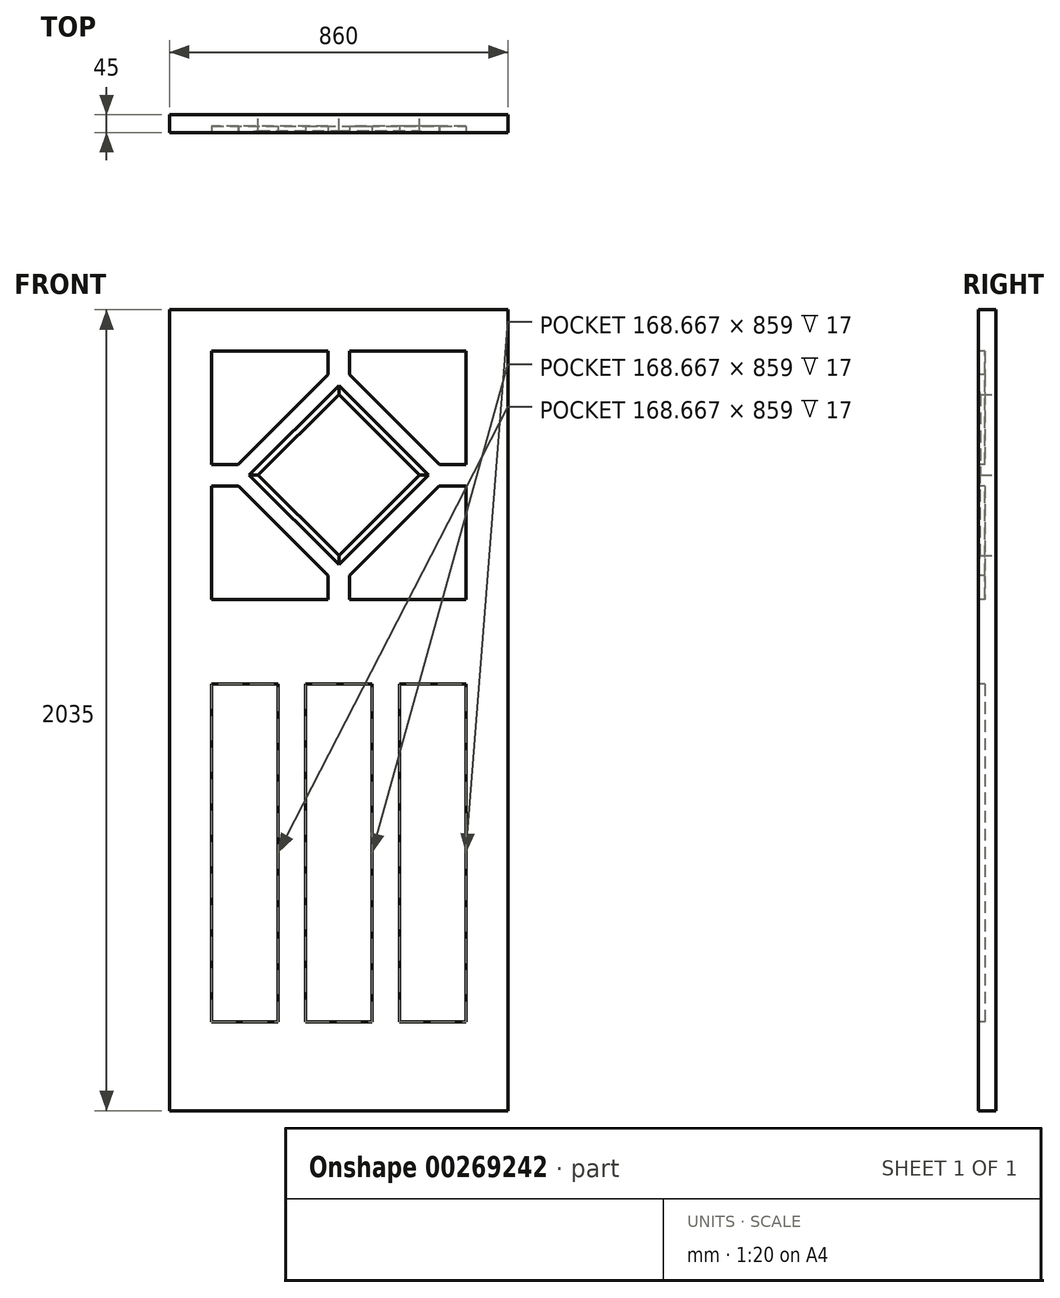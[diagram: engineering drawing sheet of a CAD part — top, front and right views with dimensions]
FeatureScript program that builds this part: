
annotation { "Feature Type Name" : "Feature", "Feature Type Description" : "" }
export const myFeature = defineFeature(function(context is Context, id is Id, definition is map)
    precondition{}
    {
        {
            var Q0;
            Q0=qCreatedBy(makeId("Front.planeOp"),FACE);
            var sketch = newSketch(context, id + "F0", { "sketchPlane" : qUnion([Q0])});
            skLineSegment(sketch, "E0.bottom", {"start": v(-430, 1017.5) * mm, "end": v(430, 1017.5) * mm});
            skLineSegment(sketch, "E0.top", {"start": v(-430, -1017.5) * mm, "end": v(430, -1017.5) * mm});
            skLineSegment(sketch, "E0.left", {"start": v(-430, 1017.5) * mm, "end": v(-430, -1017.5) * mm});
            skLineSegment(sketch, "E0.right", {"start": v(430, 1017.5) * mm, "end": v(430, -1017.5) * mm});
            skPoint(sketch, "E0.middle", {"position": v(0, 0) * mm});
            skLineSegment(sketch, "E1", {"start": v(0, 392.38) * mm, "end": v(-205.06, 597.44) * mm});
            skLineSegment(sketch, "E2", {"start": v(-205.06, 597.44) * mm, "end": v(0, 802.5) * mm});
            skLineSegment(sketch, "E3", {"start": v(0, 802.5) * mm, "end": v(205.06, 597.44) * mm});
            skLineSegment(sketch, "E4", {"start": v(205.06, 597.44) * mm, "end": v(0, 392.38) * mm});
            skSolve(sketch);
        }
        {
            var Q0;
            Q0=makeQuery(id+"F0.imprint","IMPRINT",FACE,{"disambiguationData":[TD([[makeQuery(id+"F0.imprint","IMPRINT",EDGE,{"derivedFrom":sQuery(id+"F0.wireOp",EDGE,"E0.bottom")}),-1.0]])]});
            extrude(context, id + "F1", {"entities" : qUnion([Q0]), "endBound" : BoundingType.SYMMETRIC, "depth" : 45 * mm});
        }
        {
            var Q0;
            Q0=makeQuery(id+"F1.opExtrude","CAP_FACE",FACE,{"disambiguationData":[OSD([sQuery(id+"F0.wireOp",EDGE,"E0.bottom"),sQuery(id+"F0.wireOp",EDGE,"E0.top"),sQuery(id+"F0.wireOp",EDGE,"E0.left"),sQuery(id+"F0.wireOp",EDGE,"E0.right"),sQuery(id+"F0.wireOp",EDGE,"E1"),sQuery(id+"F0.wireOp",EDGE,"E2"),sQuery(id+"F0.wireOp",EDGE,"E3"),sQuery(id+"F0.wireOp",EDGE,"E4")])],"isStart":false});
            var sketch = newSketch(context, id + "F2", { "sketchPlane" : qUnion([Q0])});
            skLineSegment(sketch, "E5", {"start": v(-323, 624.5) * mm, "end": v(-323, 912.5) * mm});
            skLineSegment(sketch, "E6", {"start": v(-323, 912.5) * mm, "end": v(-27.5, 912.5) * mm});
            skLineSegment(sketch, "E7", {"start": v(-27.5, 912.5) * mm, "end": v(-27.5, 852.78) * mm});
            skLineSegment(sketch, "E8", {"start": v(-27.5, 852.78) * mm, "end": v(-255.78, 624.5) * mm});
            skLineSegment(sketch, "E9", {"start": v(-255.78, 624.5) * mm, "end": v(-323, 624.5) * mm});
            skLineSegment(sketch, "E10", {"start": v(27.5, 912.5) * mm, "end": v(27.5, 852.78) * mm});
            skLineSegment(sketch, "E11", {"start": v(27.5, 852.78) * mm, "end": v(255.78, 624.5) * mm});
            skLineSegment(sketch, "E12", {"start": v(255.78, 624.5) * mm, "end": v(323, 624.5) * mm});
            skLineSegment(sketch, "E13", {"start": v(323, 624.5) * mm, "end": v(323, 912.5) * mm});
            skLineSegment(sketch, "E14", {"start": v(323, 912.5) * mm, "end": v(27.5, 912.5) * mm});
            skLineSegment(sketch, "E15", {"start": v(-323, 569.5) * mm, "end": v(-323, 281.5) * mm});
            skLineSegment(sketch, "E16", {"start": v(-323, 281.5) * mm, "end": v(-27.5, 281.5) * mm});
            skLineSegment(sketch, "E17", {"start": v(-27.5, 281.5) * mm, "end": v(-27.5, 342.1) * mm});
            skLineSegment(sketch, "E18", {"start": v(-27.5, 342.1) * mm, "end": v(-254.9, 569.5) * mm});
            skLineSegment(sketch, "E19", {"start": v(-254.9, 569.5) * mm, "end": v(-323, 569.5) * mm});
            skLineSegment(sketch, "E20", {"start": v(27.5, 281.5) * mm, "end": v(323, 281.5) * mm});
            skLineSegment(sketch, "E21", {"start": v(323, 281.5) * mm, "end": v(323, 569.5) * mm});
            skLineSegment(sketch, "E22", {"start": v(323, 569.5) * mm, "end": v(254.9, 569.5) * mm});
            skLineSegment(sketch, "E23", {"start": v(254.9, 569.5) * mm, "end": v(27.5, 342.1) * mm});
            skLineSegment(sketch, "E24", {"start": v(27.5, 342.1) * mm, "end": v(27.5, 281.5) * mm});
            skLineSegment(sketch, "E25.bottom", {"start": v(-323, 66.5) * mm, "end": v(-154.33, 66.5) * mm});
            skLineSegment(sketch, "E25.top", {"start": v(-323, -792.5) * mm, "end": v(-154.33, -792.5) * mm});
            skLineSegment(sketch, "E25.left", {"start": v(-323, 66.5) * mm, "end": v(-323, -792.5) * mm});
            skLineSegment(sketch, "E25.right", {"start": v(-154.33, 66.5) * mm, "end": v(-154.33, -792.5) * mm});
            skLineSegment(sketch, "E26.bottom", {"start": v(323, 66.5) * mm, "end": v(154.33, 66.5) * mm});
            skLineSegment(sketch, "E26.top", {"start": v(323, -792.5) * mm, "end": v(154.33, -792.5) * mm});
            skLineSegment(sketch, "E26.left", {"start": v(323, 66.5) * mm, "end": v(323, -792.5) * mm});
            skLineSegment(sketch, "E26.right", {"start": v(154.33, 66.5) * mm, "end": v(154.33, -792.5) * mm});
            skLineSegment(sketch, "E27.bottom", {"start": v(-84.33, 66.5) * mm, "end": v(84.33, 66.5) * mm});
            skLineSegment(sketch, "E27.top", {"start": v(-84.33, -792.5) * mm, "end": v(84.33, -792.5) * mm});
            skLineSegment(sketch, "E27.left", {"start": v(-84.33, 66.5) * mm, "end": v(-84.33, -792.5) * mm});
            skLineSegment(sketch, "E27.right", {"start": v(84.33, 66.5) * mm, "end": v(84.33, -792.5) * mm});
            skSolve(sketch);
        }
        {
            var Q0;
            Q0=makeQuery(id+"F2.imprint","IMPRINT",FACE,{"disambiguationData":[TD([[makeQuery(id+"F2.imprint","IMPRINT",EDGE,{"derivedFrom":sQuery(id+"F2.wireOp",EDGE,"E5")}),-1.0]])]});
            var Q1;
            Q1=makeQuery(id+"F2.imprint","IMPRINT",FACE,{"disambiguationData":[TD([[makeQuery(id+"F2.imprint","IMPRINT",EDGE,{"derivedFrom":sQuery(id+"F2.wireOp",EDGE,"E10")}),1.0]])]});
            var Q2;
            Q2=makeQuery(id+"F2.imprint","IMPRINT",FACE,{"disambiguationData":[TD([[makeQuery(id+"F2.imprint","IMPRINT",EDGE,{"derivedFrom":sQuery(id+"F2.wireOp",EDGE,"E20")}),1.0]])]});
            var Q3;
            Q3=makeQuery(id+"F2.imprint","IMPRINT",FACE,{"disambiguationData":[TD([[makeQuery(id+"F2.imprint","IMPRINT",EDGE,{"derivedFrom":sQuery(id+"F2.wireOp",EDGE,"E15")}),1.0]])]});
            var Q4;
            Q4=makeQuery(id+"F2.imprint","IMPRINT",FACE,{"disambiguationData":[TD([[makeQuery(id+"F2.imprint","IMPRINT",EDGE,{"derivedFrom":sQuery(id+"F2.wireOp",EDGE,"E25.bottom")}),-1.0]])]});
            var Q5;
            Q5=makeQuery(id+"F2.imprint","IMPRINT",FACE,{"disambiguationData":[TD([[makeQuery(id+"F2.imprint","IMPRINT",EDGE,{"derivedFrom":sQuery(id+"F2.wireOp",EDGE,"E27.bottom")}),-1.0]])]});
            var Q6;
            Q6=makeQuery(id+"F2.imprint","IMPRINT",FACE,{"disambiguationData":[TD([[makeQuery(id+"F2.imprint","IMPRINT",EDGE,{"derivedFrom":sQuery(id+"F2.wireOp",EDGE,"E26.bottom")}),1.0]])]});
            extrude(context, id + "F3", {"entities" : qUnion([Q0, Q1, Q2, Q3, Q4, Q5, Q6]), "operationType" : NewBodyOperationType.REMOVE, "oppositeDirection" : true, "depth" : 17 * mm});
        }
        {
            var Q0;
            Q0=makeQuery(id+"F3.boolean.opBoolean","COPY",EDGE,{"derivedFrom":makeQuery(id+"F3.opExtrude","CAP_EDGE",EDGE,{"disambiguationData":[OSD([sQuery(id+"F2.wireOp",EDGE,"E25.left")])],"isStart":true})});
            var Q1;
            Q1=makeQuery(id+"F3.boolean.opBoolean","COPY",EDGE,{"derivedFrom":makeQuery(id+"F3.opExtrude","CAP_EDGE",EDGE,{"disambiguationData":[OSD([sQuery(id+"F2.wireOp",EDGE,"E25.bottom")])],"isStart":true})});
            var Q2;
            Q2=makeQuery(id+"F3.boolean.opBoolean","COPY",EDGE,{"derivedFrom":makeQuery(id+"F3.opExtrude","CAP_EDGE",EDGE,{"disambiguationData":[OSD([sQuery(id+"F2.wireOp",EDGE,"E25.right")])],"isStart":true})});
            var Q3;
            Q3=makeQuery(id+"F3.boolean.opBoolean","COPY",EDGE,{"derivedFrom":makeQuery(id+"F3.opExtrude","CAP_EDGE",EDGE,{"disambiguationData":[OSD([sQuery(id+"F2.wireOp",EDGE,"E25.top")])],"isStart":true})});
            var Q4;
            Q4=makeQuery(id+"F3.boolean.opBoolean","COPY",EDGE,{"derivedFrom":makeQuery(id+"F3.opExtrude","CAP_EDGE",EDGE,{"disambiguationData":[OSD([sQuery(id+"F2.wireOp",EDGE,"E27.left")])],"isStart":true})});
            var Q5;
            Q5=makeQuery(id+"F3.boolean.opBoolean","COPY",EDGE,{"derivedFrom":makeQuery(id+"F3.opExtrude","CAP_EDGE",EDGE,{"disambiguationData":[OSD([sQuery(id+"F2.wireOp",EDGE,"E27.top")])],"isStart":true})});
            var Q6;
            Q6=makeQuery(id+"F3.boolean.opBoolean","COPY",EDGE,{"derivedFrom":makeQuery(id+"F3.opExtrude","CAP_EDGE",EDGE,{"disambiguationData":[OSD([sQuery(id+"F2.wireOp",EDGE,"E27.right")])],"isStart":true})});
            var Q7;
            Q7=makeQuery(id+"F3.boolean.opBoolean","COPY",EDGE,{"derivedFrom":makeQuery(id+"F3.opExtrude","CAP_EDGE",EDGE,{"disambiguationData":[OSD([sQuery(id+"F2.wireOp",EDGE,"E26.right")])],"isStart":true})});
            var Q8;
            Q8=makeQuery(id+"F3.boolean.opBoolean","COPY",EDGE,{"derivedFrom":makeQuery(id+"F3.opExtrude","CAP_EDGE",EDGE,{"disambiguationData":[OSD([sQuery(id+"F2.wireOp",EDGE,"E26.top")])],"isStart":true})});
            var Q9;
            Q9=makeQuery(id+"F3.boolean.opBoolean","COPY",EDGE,{"derivedFrom":makeQuery(id+"F3.opExtrude","CAP_EDGE",EDGE,{"disambiguationData":[OSD([sQuery(id+"F2.wireOp",EDGE,"E26.left")])],"isStart":true})});
            var Q10;
            Q10=makeQuery(id+"F3.boolean.opBoolean","COPY",EDGE,{"derivedFrom":makeQuery(id+"F3.opExtrude","CAP_EDGE",EDGE,{"disambiguationData":[OSD([sQuery(id+"F2.wireOp",EDGE,"E26.bottom")])],"isStart":true})});
            var Q11;
            Q11=makeQuery(id+"F3.boolean.opBoolean","COPY",EDGE,{"derivedFrom":makeQuery(id+"F3.opExtrude","CAP_EDGE",EDGE,{"disambiguationData":[OSD([sQuery(id+"F2.wireOp",EDGE,"E27.bottom")])],"isStart":true})});
            var Q12;
            Q12=makeQuery(id+"F3.boolean.opBoolean","COPY",EDGE,{"derivedFrom":makeQuery(id+"F3.opExtrude","CAP_EDGE",EDGE,{"disambiguationData":[OSD([sQuery(id+"F2.wireOp",EDGE,"E20")])],"isStart":true})});
            var Q13;
            Q13=makeQuery(id+"F3.boolean.opBoolean","COPY",EDGE,{"derivedFrom":makeQuery(id+"F3.opExtrude","CAP_EDGE",EDGE,{"disambiguationData":[OSD([sQuery(id+"F2.wireOp",EDGE,"E21")])],"isStart":true})});
            var Q14;
            Q14=makeQuery(id+"F3.boolean.opBoolean","COPY",EDGE,{"derivedFrom":makeQuery(id+"F3.opExtrude","CAP_EDGE",EDGE,{"disambiguationData":[OSD([sQuery(id+"F2.wireOp",EDGE,"E22")])],"isStart":true})});
            var Q15;
            Q15=makeQuery(id+"F3.boolean.opBoolean","COPY",EDGE,{"derivedFrom":makeQuery(id+"F3.opExtrude","CAP_EDGE",EDGE,{"disambiguationData":[OSD([sQuery(id+"F2.wireOp",EDGE,"E12")])],"isStart":true})});
            var Q16;
            Q16=makeQuery(id+"F3.boolean.opBoolean","COPY",EDGE,{"derivedFrom":makeQuery(id+"F3.opExtrude","CAP_EDGE",EDGE,{"disambiguationData":[OSD([sQuery(id+"F2.wireOp",EDGE,"E13")])],"isStart":true})});
            var Q17;
            Q17=makeQuery(id+"F3.boolean.opBoolean","COPY",EDGE,{"derivedFrom":makeQuery(id+"F3.opExtrude","CAP_EDGE",EDGE,{"disambiguationData":[OSD([sQuery(id+"F2.wireOp",EDGE,"E17")])],"isStart":true})});
            var Q18;
            Q18=makeQuery(id+"F3.boolean.opBoolean","COPY",EDGE,{"derivedFrom":makeQuery(id+"F3.opExtrude","CAP_EDGE",EDGE,{"disambiguationData":[OSD([sQuery(id+"F2.wireOp",EDGE,"E16")])],"isStart":true})});
            var Q19;
            Q19=makeQuery(id+"F3.boolean.opBoolean","COPY",EDGE,{"derivedFrom":makeQuery(id+"F3.opExtrude","CAP_EDGE",EDGE,{"disambiguationData":[OSD([sQuery(id+"F2.wireOp",EDGE,"E8")])],"isStart":true})});
            var Q20;
            Q20=makeQuery(id+"F3.boolean.opBoolean","COPY",EDGE,{"derivedFrom":makeQuery(id+"F3.opExtrude","CAP_EDGE",EDGE,{"disambiguationData":[OSD([sQuery(id+"F2.wireOp",EDGE,"E9")])],"isStart":true})});
            var Q21;
            Q21=makeQuery(id+"F3.boolean.opBoolean","COPY",EDGE,{"derivedFrom":makeQuery(id+"F3.opExtrude","CAP_EDGE",EDGE,{"disambiguationData":[OSD([sQuery(id+"F2.wireOp",EDGE,"E14")])],"isStart":true})});
            var Q22;
            Q22=makeQuery(id+"F3.boolean.opBoolean","COPY",EDGE,{"derivedFrom":makeQuery(id+"F3.opExtrude","CAP_EDGE",EDGE,{"disambiguationData":[OSD([sQuery(id+"F2.wireOp",EDGE,"E23")])],"isStart":true})});
            var Q23;
            Q23=makeQuery(id+"F3.boolean.opBoolean","COPY",EDGE,{"derivedFrom":makeQuery(id+"F3.opExtrude","CAP_EDGE",EDGE,{"disambiguationData":[OSD([sQuery(id+"F2.wireOp",EDGE,"E7")])],"isStart":true})});
            var Q24;
            Q24=makeQuery(id+"F3.boolean.opBoolean","COPY",EDGE,{"derivedFrom":makeQuery(id+"F3.opExtrude","CAP_EDGE",EDGE,{"disambiguationData":[OSD([sQuery(id+"F2.wireOp",EDGE,"E6")])],"isStart":true})});
            var Q25;
            Q25=makeQuery(id+"F3.boolean.opBoolean","COPY",EDGE,{"derivedFrom":makeQuery(id+"F3.opExtrude","CAP_EDGE",EDGE,{"disambiguationData":[OSD([sQuery(id+"F2.wireOp",EDGE,"E19")])],"isStart":true})});
            var Q26;
            Q26=makeQuery(id+"F3.boolean.opBoolean","COPY",EDGE,{"derivedFrom":makeQuery(id+"F3.opExtrude","CAP_EDGE",EDGE,{"disambiguationData":[OSD([sQuery(id+"F2.wireOp",EDGE,"E18")])],"isStart":true})});
            var Q27;
            Q27=makeQuery(id+"F3.boolean.opBoolean","COPY",EDGE,{"derivedFrom":makeQuery(id+"F3.opExtrude","CAP_EDGE",EDGE,{"disambiguationData":[OSD([sQuery(id+"F2.wireOp",EDGE,"E15")])],"isStart":true})});
            var Q28;
            Q28=makeQuery(id+"F3.boolean.opBoolean","COPY",EDGE,{"derivedFrom":makeQuery(id+"F3.opExtrude","CAP_EDGE",EDGE,{"disambiguationData":[OSD([sQuery(id+"F2.wireOp",EDGE,"E5")])],"isStart":true})});
            var Q29;
            Q29=makeQuery(id+"F3.boolean.opBoolean","COPY",EDGE,{"derivedFrom":makeQuery(id+"F3.opExtrude","CAP_EDGE",EDGE,{"disambiguationData":[OSD([sQuery(id+"F2.wireOp",EDGE,"E10")])],"isStart":true})});
            var Q30;
            Q30=makeQuery(id+"F3.boolean.opBoolean","COPY",EDGE,{"derivedFrom":makeQuery(id+"F3.opExtrude","CAP_EDGE",EDGE,{"disambiguationData":[OSD([sQuery(id+"F2.wireOp",EDGE,"E11")])],"isStart":true})});
            var Q31;
            Q31=makeQuery(id+"F3.boolean.opBoolean","COPY",EDGE,{"derivedFrom":makeQuery(id+"F3.opExtrude","CAP_EDGE",EDGE,{"disambiguationData":[OSD([sQuery(id+"F2.wireOp",EDGE,"E24")])],"isStart":true})});
            var Q32;
            Q32=makeQuery(id+"F1.opExtrude","CAP_EDGE",EDGE,{"disambiguationData":[OSD([sQuery(id+"F0.wireOp",EDGE,"E1")])],"isStart":false});
            var Q33;
            Q33=makeQuery(id+"F1.opExtrude","CAP_EDGE",EDGE,{"disambiguationData":[OSD([sQuery(id+"F0.wireOp",EDGE,"E2")])],"isStart":false});
            var Q34;
            Q34=makeQuery(id+"F1.opExtrude","CAP_EDGE",EDGE,{"disambiguationData":[OSD([sQuery(id+"F0.wireOp",EDGE,"E3")])],"isStart":false});
            var Q35;
            Q35=makeQuery(id+"F1.opExtrude","CAP_EDGE",EDGE,{"disambiguationData":[OSD([sQuery(id+"F0.wireOp",EDGE,"E4")])],"isStart":false});
            chamfer(context, id + "F4", {"entities" : qUnion([Q0, Q1, Q2, Q3, Q4, Q5, Q6, Q7, Q8, Q9, Q10, Q11, Q12, Q13, Q14, Q15, Q16, Q17, Q18, Q19, Q20, Q21, Q22, Q23, Q24, Q25, Q26, Q27, Q28, Q29, Q30, Q31, Q32, Q33, Q34, Q35]), "chamferType" : ChamferType.TWO_OFFSETS, "width1" : 16 * mm, "oppositeDirection" : false, "width2" : 5 * mm, "tangentPropagation" : true});
        }
    });
